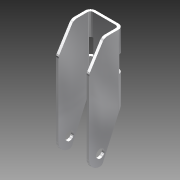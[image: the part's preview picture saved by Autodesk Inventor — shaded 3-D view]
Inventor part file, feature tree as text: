
AUTODESK INVENTOR PART (.ipt)
format: ipt  version: 2011 (Build 150239000, 239)  size: 275,968 bytes
history: native  units: mm (DEFAULTED — no unit token found)
features: sheet_metal_op x7, sketch x6, other x6, reference x3, plane x2, extrude x1, projected_geometry x1
ambient origin geometry x8: Origin, YZ Plane, XZ Plane, XY Plane, X Axis, Y Axis, Z Axis, Center Point
bodies: Solid1 (feature_tree)
feature tree (26):
  sheet_metal_op  "Face1"
  plane  "Work Plane1"
  sheet_metal_op  "Face2"
  plane  "Work Plane2"
  sheet_metal_op  "Face3"
  sheet_metal_op  "Bend3"
  sheet_metal_op  "Bend4"
  extrude  "Extrusion2"  Depth=10.068945mm
  sketch  "Sketch1"  dims[d0=38.1mm d1=10.068945mm]
  other  "Plate1"
  sketch  "Sketch2"  dims[d2=1.4986mm]
  reference  "Reference1"
  reference  "Reference2"
  reference  "Reference3"
  other  "Plate2"
  sheet_metal_op  "Bend1"
  sketch  "Sketch3"  dims[d3=21.293017mm]
  projected_geometry  "Projected Loop1"
  other  "Plate3"
  sheet_metal_op  "Bend2"
  sketch  "Sketch5"  dims[d4=1.5748mm]
  sketch  "Sketch7"  dims[d5=27.227136mm]
  sketch  "Sketch8"  dims[d6=1.4986mm d7=1.4986mm d8=0.7493mm d9=2.9972mm d10=1.4986mm d11=1.4986mm d12=1.4986mm d13=0.7493mm d14=2.9972mm d15=1.4986mm d16=1.4986mm d17=0.7493mm d18=2.9972mm d19=1.4986mm d20=1.4986mm d21=1.4986mm d22=0.7493mm d23=2.9972mm d24=1.4986mm d25=1.4986mm d26=3.175mm d27=3.175mm d33=9.525mm d34=2.3876mm d35=15.875mm d36=3.175mm d37=0.0mm d40=1.4986mm d41=0.0mm d42=3.175mm d43=0.0mm d44=1.5748mm]
  other  "Cut1"
  other  "Cut3"
  other  "Definition1"
